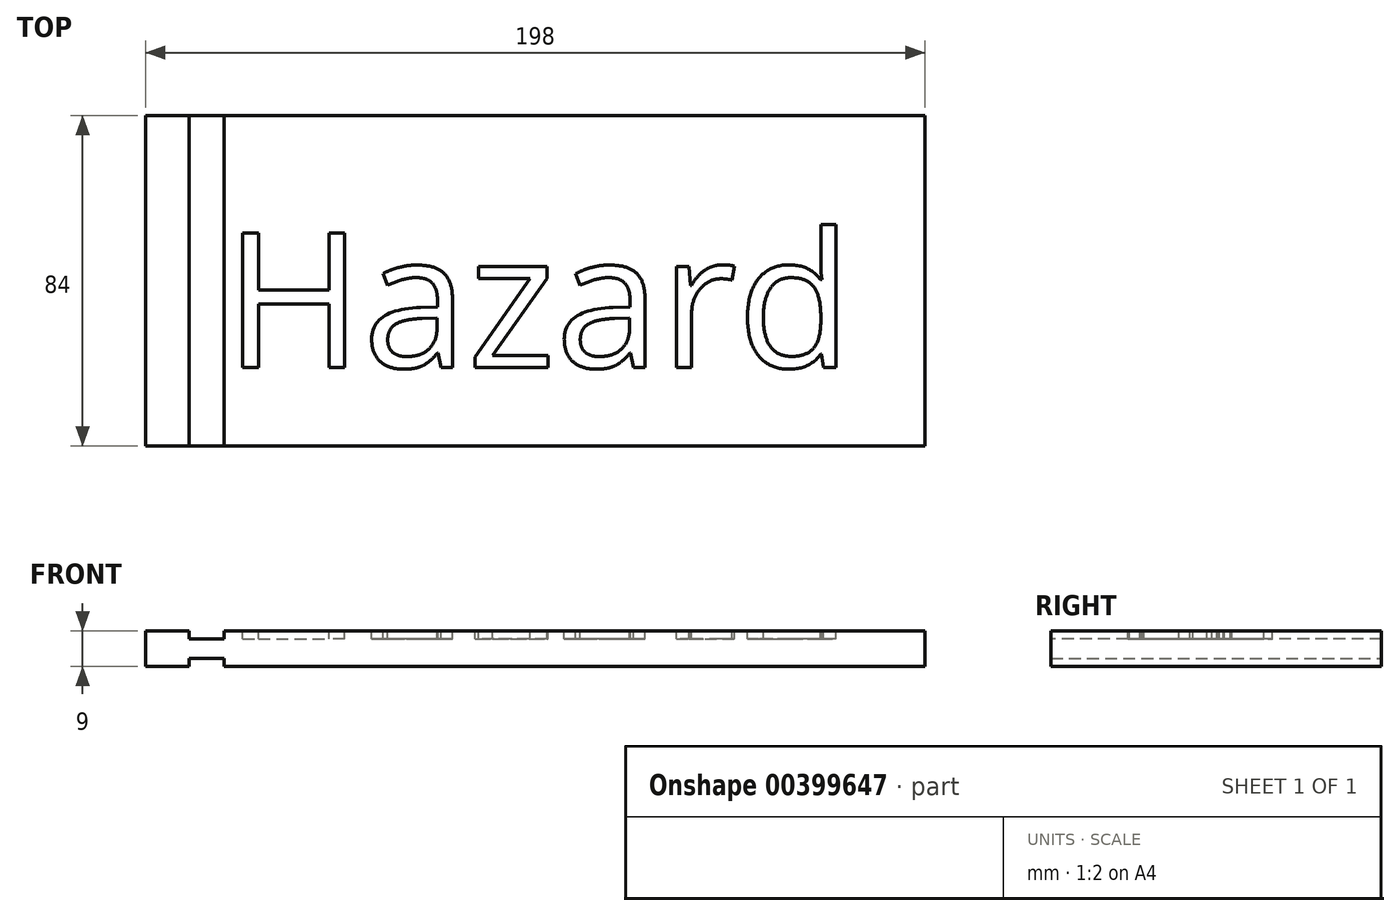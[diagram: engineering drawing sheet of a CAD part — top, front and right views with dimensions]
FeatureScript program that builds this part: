
annotation { "Feature Type Name" : "Feature", "Feature Type Description" : "" }
export const myFeature = defineFeature(function(context is Context, id is Id, definition is map)
    precondition{}
    {
        {
            var Q0;
            Q0=qCreatedBy(makeId("Top.planeOp"),FACE);
            var sketch = newSketch(context, id + "F0", { "sketchPlane" : qUnion([Q0])});
            skLineSegment(sketch, "E0.bottom", {"start": v(-99, 42) * mm, "end": v(99, 42) * mm});
            skLineSegment(sketch, "E0.top", {"start": v(-99, -42) * mm, "end": v(99, -42) * mm});
            skLineSegment(sketch, "E0.left", {"start": v(-99, 42) * mm, "end": v(-99, -42) * mm});
            skLineSegment(sketch, "E0.right", {"start": v(99, 42) * mm, "end": v(99, -42) * mm});
            skPoint(sketch, "E0.middle", {"position": v(0, 0) * mm});
            skSolve(sketch);
        }
        {
            var Q0;
            Q0=makeQuery(id+"F0.imprint","IMPRINT",FACE,{"disambiguationData":[TD([[makeQuery(id+"F0.imprint","IMPRINT",EDGE,{"derivedFrom":sQuery(id+"F0.wireOp",EDGE,"E0.bottom")}),-1.0]])]});
            extrude(context, id + "F1", {"entities" : qUnion([Q0]), "depth" : 9 * mm});
        }
        {
            var Q0;
            Q0=makeQuery(id+"F1.opExtrude","CAP_FACE",FACE,{"disambiguationData":[OSD([sQuery(id+"F0.wireOp",EDGE,"E0.bottom"),sQuery(id+"F0.wireOp",EDGE,"E0.top"),sQuery(id+"F0.wireOp",EDGE,"E0.left"),sQuery(id+"F0.wireOp",EDGE,"E0.right")])],"isStart":false});
            var sketch = newSketch(context, id + "F2", { "sketchPlane" : qUnion([Q0])});
            skLineSegment(sketch, "E1.bottom", {"start": v(-88, 42) * mm, "end": v(-79, 42) * mm});
            skLineSegment(sketch, "E1.top", {"start": v(-88, -42) * mm, "end": v(-79, -42) * mm});
            skLineSegment(sketch, "E1.left", {"start": v(-88, 42) * mm, "end": v(-88, -42) * mm});
            skLineSegment(sketch, "E1.right", {"start": v(-79, 42) * mm, "end": v(-79, -42) * mm});
            skLineSegment(sketch, "E2.bottom", {"start": v(-79, -22) * mm, "end": v(79, -22) * mm, "construction": true});
            skLineSegment(sketch, "E2.top", {"start": v(-79, 22) * mm, "end": v(79, 22) * mm, "construction": true});
            skLineSegment(sketch, "E2.left", {"start": v(-79, -22) * mm, "end": v(-79, 22) * mm, "construction": true});
            skLineSegment(sketch, "E2.right", {"start": v(79, -22) * mm, "end": v(79, 22) * mm, "construction": true});
            skText(sketch, "E3", { "text": "Hazard", "fontName": "OpenSans-Regular.ttf"});
            const initialGuessF2  = {"E3": [-0.079, -0.022, 1, 0, 0.0344]};
            skSetInitialGuess(sketch, initialGuessF2);
            skSolve(sketch);
        }
        {
            var Q0;
            Q0=makeQuery(id+"F2.imprint","IMPRINT",FACE,{"disambiguationData":[TD([[makeQuery(id+"F2.imprint","IMPRINT",EDGE,{"derivedFrom":sQuery(id+"F2.wireOp",EDGE,"E3.sketch_text.stroke-0")}),-1.0]])]});
            var Q1;
            Q1=makeQuery(id+"F2.imprint","IMPRINT",FACE,{"disambiguationData":[TD([[makeQuery(id+"F2.imprint","IMPRINT",EDGE,{"derivedFrom":sQuery(id+"F2.wireOp",EDGE,"E3.sketch_text.stroke-12")}),-1.0]])]});
            var Q2;
            Q2=makeQuery(id+"F2.imprint","IMPRINT",FACE,{"disambiguationData":[TD([[makeQuery(id+"F2.imprint","IMPRINT",EDGE,{"derivedFrom":sQuery(id+"F2.wireOp",EDGE,"E3.sketch_text.stroke-39")}),-1.0]])]});
            var Q3;
            Q3=makeQuery(id+"F2.imprint","IMPRINT",FACE,{"disambiguationData":[TD([[makeQuery(id+"F2.imprint","IMPRINT",EDGE,{"derivedFrom":sQuery(id+"F2.wireOp",EDGE,"E3.sketch_text.stroke-49")}),-1.0]])]});
            var Q4;
            Q4=makeQuery(id+"F2.imprint","IMPRINT",FACE,{"disambiguationData":[TD([[makeQuery(id+"F2.imprint","IMPRINT",EDGE,{"derivedFrom":sQuery(id+"F2.wireOp",EDGE,"E3.sketch_text.stroke-76")}),-1.0]])]});
            var Q5;
            Q5=makeQuery(id+"F2.imprint","IMPRINT",FACE,{"disambiguationData":[TD([[makeQuery(id+"F2.imprint","IMPRINT",EDGE,{"derivedFrom":sQuery(id+"F2.wireOp",EDGE,"E3.sketch_text.stroke-89")}),-1.0]])]});
            extrude(context, id + "F3", {"entities" : qUnion([Q0, Q1, Q2, Q3, Q4, Q5]), "operationType" : NewBodyOperationType.REMOVE, "oppositeDirection" : true, "depth" : 2 * mm});
        }
        {
            var Q0;
            Q0=makeQuery(id+"F2.imprint","IMPRINT",FACE,{"disambiguationData":[TD([[makeQuery(id+"F2.imprint","IMPRINT",EDGE,{"derivedFrom":sQuery(id+"F2.wireOp",EDGE,"E1.bottom")}),-1.0]])]});
            extrude(context, id + "F4", {"entities" : qUnion([Q0]), "operationType" : NewBodyOperationType.REMOVE, "oppositeDirection" : true, "depth" : 2 * mm});
        }
        {
            var Q0;
            {var subQ0=sQuery(id+"F0.wireOp",EDGE,"E0.left");var subQ1=sQuery(id+"F0.wireOp",EDGE,"E0.bottom");var subQ2=sQuery(id+"F0.wireOp",EDGE,"E0.right");var subQ3=sQuery(id+"F0.wireOp",EDGE,"E0.top");Q0=makeQuery(id+"F3.boolean.opBoolean","SPLIT",FACE,{"disambiguationData":[TD([makeQuery(id+"F1.opExtrude","SWEPT_FACE",FACE,{"disambiguationData":[OSD([subQ1])]})])],"derivedFrom":makeQuery(id+"F1.opExtrude","CAP_FACE",FACE,{"disambiguationData":[OSD([subQ1,subQ3,subQ0,subQ2])],"isStart":true})});}
            var sketch = newSketch(context, id + "F5", { "sketchPlane" : qUnion([Q0])});
            skLineSegment(sketch, "E4.0.0", {"start": v(-79, 42) * mm, "end": v(-79, -42) * mm});
            skLineSegment(sketch, "E4.0.1", {"start": v(-79, -42) * mm, "end": v(-88, -42) * mm});
            skLineSegment(sketch, "E4.0.2", {"start": v(-88, -42) * mm, "end": v(-88, 42) * mm});
            skLineSegment(sketch, "E4.0.3", {"start": v(-88, 42) * mm, "end": v(-79, 42) * mm});
            skSolve(sketch);
        }
        {
            var Q0;
            Q0 = qSketchRegion(id + "F5", true);
            extrude(context, id + "F6", {"entities" : qUnion([Q0]), "operationType" : NewBodyOperationType.REMOVE, "oppositeDirection" : true, "depth" : 2 * mm});
        }
    });
